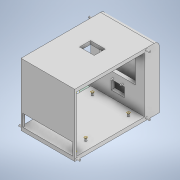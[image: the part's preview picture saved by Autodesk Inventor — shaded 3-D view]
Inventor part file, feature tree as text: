
AUTODESK INVENTOR PART (.ipt)
format: ipt  version: 2021 (Build 250183000, 183)  size: 412,672 bytes
history: native  units: mm
features: sketch x26, extrude x22, plane x9, loft x8, other x8, fillet x2
ambient origin geometry x8: Origin, YZ Plane, XZ Plane, XY Plane, X Axis, Y Axis, Z Axis, Center Point
bodies: Solid1 (feature_tree)
feature tree (75):
  extrude  "Extrusion1"  Depth=70.0mm
  sketch  "Sketch2"  dims[d2=5.0mm d3=0.0mm d11=9.1mm]
  extrude  "Extrusion2"  Depth=5.0mm
  sketch  "Sketch3"  dims[d12=9.1mm d13=2.7mm]
  plane  "Work Plane2"
  sketch  "Sketch5"  dims[d14=2.7mm d15=58.0mm]
  plane  "Work Plane3"
  sketch  "Sketch6"  dims[d16=58.0mm d18=2.7mm]
  loft  "Loft3"
  loft  "Loft4"
  extrude  "Extrusion3"  Depth=2.7mm
  plane  "Work Plane5"
  sketch  "Sketch8"  dims[d19=2.7mm d21=3.0mm d22=0.0mm]
  plane  "Work Plane6"
  loft  "Loft5"
  loft  "Loft6"
  extrude  "Extrusion4"  Depth=20.0mm TaperAngle=90.0deg
  extrude  "Extrusion6"  Depth=20.0mm TaperAngle=90.0deg
  extrude  "Extrusion7"  Depth=2.7mm
  extrude  "Extrusion8"  Depth=2.7mm
  extrude  "Extrusion9"  Depth=1.0mm
  sketch  "Sketch16"  dims[d50=1.0mm d51=0.0mm d52=90.0deg]
  extrude  "Extrusion10"  TaperAngle=0.0deg  [1 undecoded]
  extrude  "Extrusion11"  TaperAngle=0.0deg  [1 undecoded]
  plane  "Work Plane7"
  loft  "Loft7"
  plane  "Work Plane8"
  loft  "Loft8"
  extrude  "Extrusion12"  Depth=5.0mm
  sketch  "Sketch21"  dims[d67=5.0mm d68=0.0mm d69=5.0mm]
  extrude  "Extrusion13"  Depth=6.5mm
  extrude  "Extrusion14"  Depth=22.5mm
  plane  "Work Plane9"
  loft  "Loft9"
  plane  "Work Plane12"
  loft  "Loft12"
  plane  "Work Plane13"
  sketch  "Sketch27"  dims[d76=60.0mm d77=45.0mm]
  extrude  "Extrusion16"  Depth=6.0mm
  extrude  "Extrusion17"  Depth=0.1mm
  extrude  "Extrusion18"  Depth=1.9mm
  extrude  "Extrusion19"  Depth=8.0mm TaperAngle=0.0deg
  extrude  "Extrusion20"  TaperAngle=0.0deg  [1 undecoded]
  extrude  "Extrusion21"  Depth=5.0mm TaperAngle=90.0deg
  fillet  "Fillet1"  Radius=1.0mm
  extrude  "Extrusion22"  TaperAngle=0.0deg  [1 undecoded]
  extrude  "Extrusion23"  Depth=5.0mm TaperAngle=90.0deg
  fillet  "Fillet2"  Radius=4.5mm
  sketch  "Sketch32"  dims[d88=1.9mm d89=8.0mm d90=0.0mm]
  extrude  "Extrusion24"  Depth=5.0mm TaperAngle=0.0deg
  sketch  "Sketch1"  dims[d0=90.0mm d1=70.0mm]
  other  "Edges3"
  other  "Edges4"
  sketch  "Sketch9"  dims[d28=1.0mm d29=1.0mm]
  other  "Edges5"
  other  "Edges6"
  sketch  "Sketch10"  dims[d35=0.0mm d36=90.0deg d37=20.0mm d38=90.0deg]
  sketch  "Sketch12"  dims[d39=0.0mm d40=90.0deg d41=20.0mm d42=90.0deg]
  sketch  "Sketch13"  dims[d43=2.8mm d44=2.7mm]
  sketch  "Sketch14"  dims[d45=2.8mm d46=2.7mm]
  sketch  "Sketch15"  dims[d47=3.0mm d48=0.0mm d49=1.0mm]
  sketch  "Sketch17"  dims[d53=20.0mm d54=90.0deg d55=0.0mm d56=90.0deg]
  other  "Edges7"
  sketch  "Sketch19"  dims[d57=20.0mm d58=90.0deg d59=5.0mm d60=0.0mm]
  other  "Edges8"
  sketch  "Sketch20"  dims[d63=0.1mm d64=0.0mm d65=2.9mm d66=0.0mm]
  sketch  "Sketch22"  dims[d70=80.0mm d71=0.0mm d73=6.5mm]
  other  "Edges9"
  sketch  "Sketch25"  dims[d74=22.5mm d75=22.5mm]
  other  "Edges12"
  sketch  "Sketch28"  dims[d78=5.0mm d79=3.0mm]
  sketch  "Sketch29"  dims[d80=3.0mm d81=6.0mm]
  sketch  "Sketch30"  dims[d82=80.0mm d83=0.0mm d85=0.1mm]
  sketch  "Sketch31"  dims[d86=1.9mm d87=1.9mm]
  sketch  "Sketch33"  dims[d91=1.0mm d92=0.0mm d93=90.0deg d94=20.0mm d95=90.0deg d96=1.0mm d97=0.0mm d98=90.0deg d99=20.0mm d100=90.0deg d101=4.5mm d102=95.0mm d103=0.0mm d104=26.5mm d106=20.0mm d107=18.0mm d108=20.0mm d109=2.5mm d110=2.5mm d111=6.0mm d117=10.0mm d118=0.0mm d119=6.5mm d120=0.0mm d121=0.5mm d122=0.0mm d123=90.0deg d124=20.0mm d125=90.0deg d136=0.5mm d137=0.0mm d138=90.0deg d139=20.0mm d140=90.0deg d144=1.25mm d145=2.5mm d146=2.5mm d147=180.0deg d148=2.5mm d149=2.5mm d150=2.5mm d151=0.0mm d152=2.5mm d153=2.5mm d154=2.5mm d155=90.0deg d156=2.5mm d157=2.5mm d158=2.5mm d159=2.5mm d160=4.5mm d161=0.0mm d162=5.0mm d163=0.0mm d164=0.5mm d165=0.0mm d166=2.5mm d167=59.0mm d168=0.0mm d169=2.5mm d170=2.5mm d171=20.0mm d172=0.0mm d173=15.24mm d174=2.5mm d177=6.0mm d178=9.0mm d179=9.0mm d180=16.5mm d181=4.0mm d182=2.286mm d183=2.286mm d184=12.7mm d185=2.794mm d186=8.0mm d187=0.0mm d188=1.0mm d189=8.0mm d190=0.0mm d191=7.0mm d192=5.0mm d193=5.0mm d194=15.0mm d195=0.0mm d196=7.0mm d197=5.0mm d198=5.0mm d199=78.0mm d200=0.0mm]
note: 4 required parameter values undecoded (feature->parameter linkage not recoverable at this tier; creation-order binding heuristic only, values carry confidence <= 0.55)
